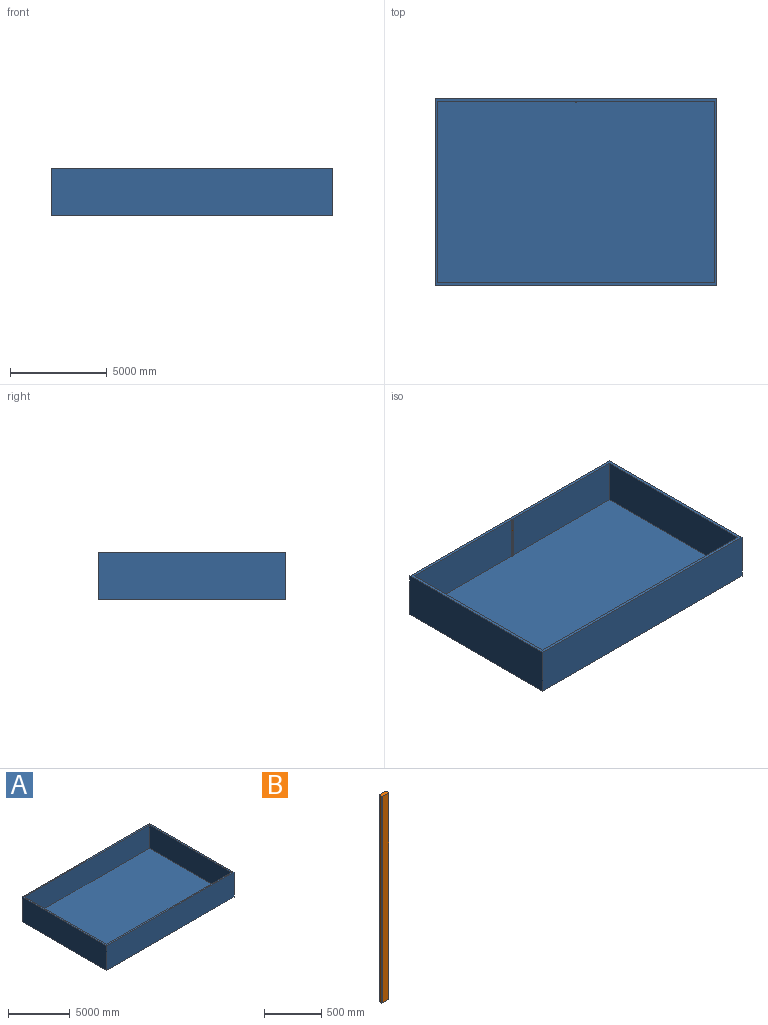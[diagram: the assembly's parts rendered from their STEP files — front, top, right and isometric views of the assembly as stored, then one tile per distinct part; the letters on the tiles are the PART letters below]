
ASSEMBLY  parts=2 mates=1
PART A: 11 faces, bbox 14537.1x9667.6x2445.1 mm
  f0: plane 14232.33x2292.71mm, normal (0,-1,0), area 32630545.4mm2, adj f1,f7,f8,f9
  f1: plane 9362.85x2292.71mm, normal (-1,0,0), area 21466250.4mm2, adj f0,f2,f8,f9
  f2: plane 14232.33x2292.71mm, normal (0,1,0), area 32630545.4mm2, adj f1,f7,f8,f9
  f3: plane 14537.13x2445.11mm, normal (0,1,0), area 35544820.9mm2, adj f4,f6,f8,f10
  f4: plane 9667.65x2445.11mm, normal (-1,0,0), area 23638416.4mm2, adj f3,f5,f8,f10
  f5: plane 14537.13x2445.11mm, normal (0,-1,0), area 35544820.9mm2, adj f4,f6,f8,f10
  f6: plane 9667.65x2445.11mm, normal (1,0,0), area 23638416.4mm2, adj f3,f5,f8,f10
  f7: plane 9362.85x2292.71mm, normal (1,0,0), area 21466250.4mm2, adj f0,f2,f8,f9
  f8: plane 14537.13x9667.65mm, normal (0,0,1), area 7284713.2mm2, adj f0,f1,f2,f3,f4,f5,f6,f7
  f9: plane 14232.33x9362.85mm, normal (0,0,1), area 133255130.9mm2, adj f0,f1,f2,f7
  f10: plane 14537.13x9667.65mm, normal (0,0,-1), area 140539844.1mm2, adj f3,f4,f5,f6
PART B: 10 faces, bbox 88.9x38.1x2216.5 mm
  f0: plane 2216.51x76.2mm, normal (0,1,0), area 168897.7mm2, adj f4,f5,f6,f9
  f1: plane 2216.51x25.4mm, normal (-1,0,0), area 56299.2mm2, adj f4,f5,f6,f7
  f2: plane 2216.51x76.2mm, normal (0,-1,0), area 168897.7mm2, adj f4,f5,f7,f8
  f3: plane 2216.51x25.4mm, normal (1,0,0), area 56299.2mm2, adj f4,f5,f8,f9
  f4: plane 88.9x38.1mm, normal (0,0,1), area 3352.5mm2, adj f0,f1,f2,f3,f6,f7,f8,f9
  f5: plane 88.9x38.1mm, normal (0,0,-1), area 3352.5mm2, adj f0,f1,f2,f3,f6,f7,f8,f9
  f6: cylinder r=6.35mm len=2216.51mm, axis (0,0,-1), area 22108.7mm2, adj f0,f1,f4,f5
  f7: cylinder r=6.35mm len=2216.51mm, axis (0,0,1), area 22108.7mm2, adj f1,f2,f4,f5
  f8: cylinder r=6.35mm len=2216.51mm, axis (0,0,-1), area 22108.7mm2, adj f2,f3,f4,f5
  f9: cylinder r=6.35mm len=2216.51mm, axis (0,0,1), area 22108.7mm2, adj f0,f3,f4,f5
PLACE A t=(7164.8,-4677.06,-1105.73)mm fixed
PLACE B rot(axis=(0,0,1),90deg) t=(48.63,4641.33,-1067.63)mm
MATE fastened A.f0 <-> B.f3  axis (0,-1,0) through (48.63,4685.78,40.62)mm
